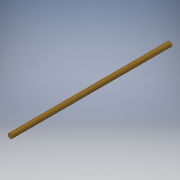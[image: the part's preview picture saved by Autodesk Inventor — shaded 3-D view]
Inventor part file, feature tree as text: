
AUTODESK INVENTOR PART (.ipt)
format: ipt  version: 2017 SP1 (Build 210196100, 196)  size: 92,160 bytes
history: native  units: in
note: dims shown in document units (in); Inventor stores cm internally (conversion verified against a paired STEP export)
features: extrude x1, sketch x1
ambient origin geometry x8: Origin, YZ Plane, XZ Plane, XY Plane, X Axis, Y Axis, Z Axis, Center Point
bodies: Solid1 (feature_tree)
feature tree (2):
  extrude  "Extrusion1"  Depth=3.937in TaperAngle=0.0deg
  sketch  "Sketch1"  dims[d0=0.1181in d1=3.937in d2=0.0in]
